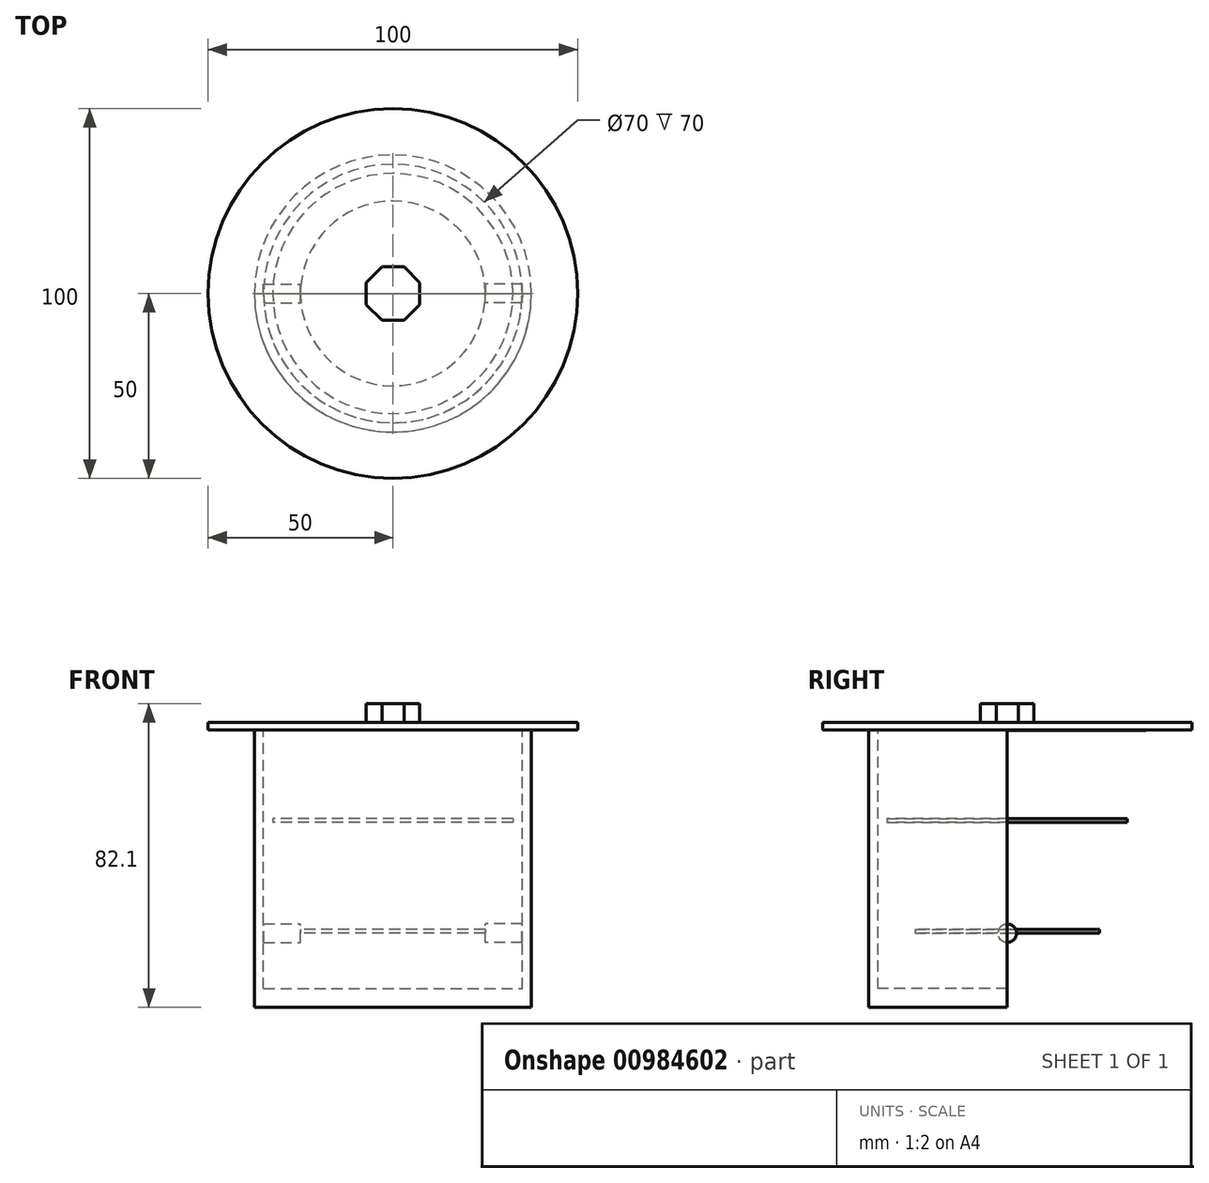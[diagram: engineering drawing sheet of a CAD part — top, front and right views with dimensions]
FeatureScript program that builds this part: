
annotation { "Feature Type Name" : "Feature", "Feature Type Description" : "" }
export const myFeature = defineFeature(function(context is Context, id is Id, definition is map)
    precondition{}
    {
        {
            var Q0;
            Q0=qCreatedBy(makeId("Top.planeOp"),FACE);
            var sketch = newSketch(context, id + "F0", { "sketchPlane" : qUnion([Q0])});
            skCircle(sketch, "E0", {"center": v(0, 0) * mm, "radius": 37.5 * mm});
            skSolve(sketch);
        }
        {
            var Q0;
            Q0 = qSketchRegion(id + "F0", true);
            extrude(context, id + "F1", {"entities" : qUnion([Q0]), "depth" : 75 * mm, "offsetDistance" : 25 * mm});
        }
        {
            var Q0;
            Q0=makeQuery(id+"F1.opExtrude","CAP_FACE",FACE,{"disambiguationData":[OSD([sQuery(id+"F0.wireOp",EDGE,"E0")])],"isStart":false});
            var sketch = newSketch(context, id + "F2", { "sketchPlane" : qUnion([Q0])});
            skCircle(sketch, "E1", {"center": v(0, 0) * mm, "radius": 35 * mm});
            skSolve(sketch);
        }
        {
            var Q0;
            Q0=makeQuery(id+"F2.imprint","IMPRINT",FACE,{"disambiguationData":[TD([[makeQuery(id+"F2.imprint","IMPRINT",EDGE,{"derivedFrom":sQuery(id+"F2.wireOp",EDGE,"E1")}),1.0]])]});
            extrude(context, id + "F3", {"entities" : qUnion([Q0]), "operationType" : NewBodyOperationType.REMOVE, "oppositeDirection" : true, "depth" : 70 * mm, "offsetDistance" : 25 * mm});
        }
        {
            var Q0;
            Q0=qCreatedBy(makeId("Front.planeOp"),FACE);
            var sketch = newSketch(context, id + "F4", { "sketchPlane" : qUnion([Q0])});
            skLineSegment(sketch, "E2.bottom", {"start": v(-73.79, 74.83) * mm, "end": v(74.86, 74.83) * mm});
            skLineSegment(sketch, "E2.top", {"start": v(-73.79, 0) * mm, "end": v(74.86, 0) * mm});
            skLineSegment(sketch, "E2.left", {"start": v(-73.79, 74.83) * mm, "end": v(-73.79, 0) * mm});
            skLineSegment(sketch, "E2.right", {"start": v(74.86, 74.83) * mm, "end": v(74.86, 0) * mm});
            skSolve(sketch);
        }
        {
            var Q0;
            Q0 = qSketchRegion(id + "F4", true);
            extrude(context, id + "F5", {"entities" : qUnion([Q0]), "operationType" : NewBodyOperationType.REMOVE, "oppositeDirection" : true, "depth" : 46 * mm, "offsetDistance" : 25 * mm});
        }
        {
            var Q0;
            Q0=qCreatedBy(makeId("Right.planeOp"),FACE);
            var sketch = newSketch(context, id + "F6", { "sketchPlane" : qUnion([Q0])});
            skLineSegment(sketch, "E3", {"start": v(0, 0) * mm, "end": v(0, 20) * mm});
            skCircle(sketch, "E4", {"center": v(0, 20) * mm, "radius": 2.5 * mm});
            skSolve(sketch);
        }
        {
            var Q0;
            Q0=makeQuery(id+"F6.imprint","IMPRINT",FACE,{"disambiguationData":[TD([[makeQuery(id+"F6.imprint","IMPRINT",EDGE,{"derivedFrom":sQuery(id+"F6.wireOp",EDGE,"E4")}),1.0]])]});
            extrude(context, id + "F7", {"entities" : qUnion([Q0]), "operationType" : NewBodyOperationType.ADD, "depth" : 35 * mm, "offsetDistance" : 25 * mm});
        }
        {
            var Q0;
            Q0=makeQuery(id+"F7.opExtrude","CAP_FACE",FACE,{"disambiguationData":[OSD([sQuery(id+"F6.wireOp",EDGE,"E4")])],"isStart":true});
            extrude(context, id + "F8", {"entities" : qUnion([Q0]), "operationType" : NewBodyOperationType.REMOVE, "oppositeDirection" : true, "depth" : 25 * mm, "offsetDistance" : 25 * mm});
        }
        {
            var Q0;
            Q0=makeQuery(id+"F6.imprint","IMPRINT",FACE,{"disambiguationData":[TD([[makeQuery(id+"F6.imprint","IMPRINT",EDGE,{"derivedFrom":sQuery(id+"F6.wireOp",EDGE,"E4")}),1.0]])]});
            extrude(context, id + "F9", {"entities" : qUnion([Q0]), "operationType" : NewBodyOperationType.ADD, "oppositeDirection" : true, "depth" : 35 * mm, "offsetDistance" : 25 * mm});
        }
        {
            var Q0;
            Q0=makeQuery(id+"F6.imprint","IMPRINT",FACE,{"disambiguationData":[TD([[makeQuery(id+"F6.imprint","IMPRINT",EDGE,{"derivedFrom":sQuery(id+"F6.wireOp",EDGE,"E4")}),1.0]])]});
            extrude(context, id + "F10", {"entities" : qUnion([Q0]), "operationType" : NewBodyOperationType.REMOVE, "oppositeDirection" : true, "depth" : 25 * mm, "offsetDistance" : 25 * mm});
        }
        {
            var Q0;
            Q0=qCreatedBy(makeId("Top.planeOp"),FACE);
            cPlane(context, id + "F11", {"entities" : qUnion([Q0]), "cplaneType" : CPlaneType.OFFSET, "offset" : 20 * mm, "width" : 150 * mm, "height" : 150 * mm});
        }
        {
            var Q0;
            Q0=qCreatedBy(id+"F11.planeOp",FACE);
            var sketch = newSketch(context, id + "F12", { "sketchPlane" : qUnion([Q0])});
            skCircle(sketch, "E5", {"center": v(0, 0) * mm, "radius": 25 * mm});
            skSolve(sketch);
        }
        {
            var Q0;
            Q0 = qSketchRegion(id + "F12", true);
            extrude(context, id + "F13", {"entities" : qUnion([Q0]), "operationType" : NewBodyOperationType.ADD, "depth" : 1 * mm, "offsetDistance" : 25 * mm});
        }
        {
            var Q0;
            Q0=qCreatedBy(id+"F11.planeOp",FACE);
            cPlane(context, id + "F14", {"entities" : qUnion([Q0]), "cplaneType" : CPlaneType.OFFSET, "offset" : 30 * mm, "width" : 150 * mm, "height" : 150 * mm});
        }
        {
            var Q0;
            Q0=qCreatedBy(id+"F14.planeOp",FACE);
            var sketch = newSketch(context, id + "F15", { "sketchPlane" : qUnion([Q0])});
            skCircle(sketch, "E6", {"center": v(0, 0) * mm, "radius": 32.5 * mm});
            skSolve(sketch);
        }
        {
            var Q0;
            Q0 = qSketchRegion(id + "F15", true);
            extrude(context, id + "F16", {"entities" : qUnion([Q0]), "depth" : 1 * mm, "offsetDistance" : 25 * mm});
        }
        {
            var Q0;
            Q0=makeQuery(id+"F1.opExtrude","CAP_FACE",FACE,{"disambiguationData":[OSD([sQuery(id+"F0.wireOp",EDGE,"E0")])],"isStart":false});
            var sketch = newSketch(context, id + "F17", { "sketchPlane" : qUnion([Q0])});
            skCircle(sketch, "E7", {"center": v(0, 0) * mm, "radius": 50 * mm});
            skSolve(sketch);
        }
        {
            var Q0;
            Q0 = qSketchRegion(id + "F17", true);
            extrude(context, id + "F18", {"entities" : qUnion([Q0]), "operationType" : NewBodyOperationType.ADD, "depth" : 2 * mm, "offsetDistance" : 25 * mm});
        }
        {
            var Q0;
            Q0=makeQuery(id+"F18.opExtrude","CAP_FACE",FACE,{"disambiguationData":[OSD([sQuery(id+"F17.wireOp",EDGE,"E7")])],"isStart":false});
            cPlane(context, id + "F19", {"entities" : qUnion([Q0]), "cplaneType" : CPlaneType.OFFSET, "offset" : 0.1 * mm, "width" : 150 * mm, "height" : 150 * mm});
        }
        {
            var Q0;
            Q0=qCreatedBy(id+"F19.planeOp",FACE);
            var sketch = newSketch(context, id + "F20", { "sketchPlane" : qUnion([Q0])});
            skCircle(sketch, "E8.cCircle", {"center": v(0, 0) * mm, "radius": 7.22 * mm, "construction": true});
            skLineSegment(sketch, "E8.0", {"start": v(7.22, 3) * mm, "end": v(7.22, -3) * mm});
            skLineSegment(sketch, "E8.1", {"start": v(7.22, -3) * mm, "end": v(3, -7.22) * mm});
            skLineSegment(sketch, "E8.2", {"start": v(3, -7.22) * mm, "end": v(-3, -7.22) * mm});
            skLineSegment(sketch, "E8.3", {"start": v(-3, -7.22) * mm, "end": v(-7.22, -3) * mm});
            skLineSegment(sketch, "E8.4", {"start": v(-7.22, -3) * mm, "end": v(-7.22, 3) * mm});
            skLineSegment(sketch, "E8.5", {"start": v(-7.22, 3) * mm, "end": v(-3, 7.22) * mm});
            skLineSegment(sketch, "E8.6", {"start": v(-3, 7.22) * mm, "end": v(3, 7.22) * mm});
            skLineSegment(sketch, "E8.7", {"start": v(3, 7.22) * mm, "end": v(7.22, 3) * mm});
            skPoint(sketch, "E8.0.midPoint", {"position": v(7.22, 0) * mm});
            skSolve(sketch);
        }
        {
            var Q0;
            Q0 = qSketchRegion(id + "F20", true);
            extrude(context, id + "F21", {"entities" : qUnion([Q0]), "depth" : 5 * mm, "offsetDistance" : 25 * mm});
        }
    });
